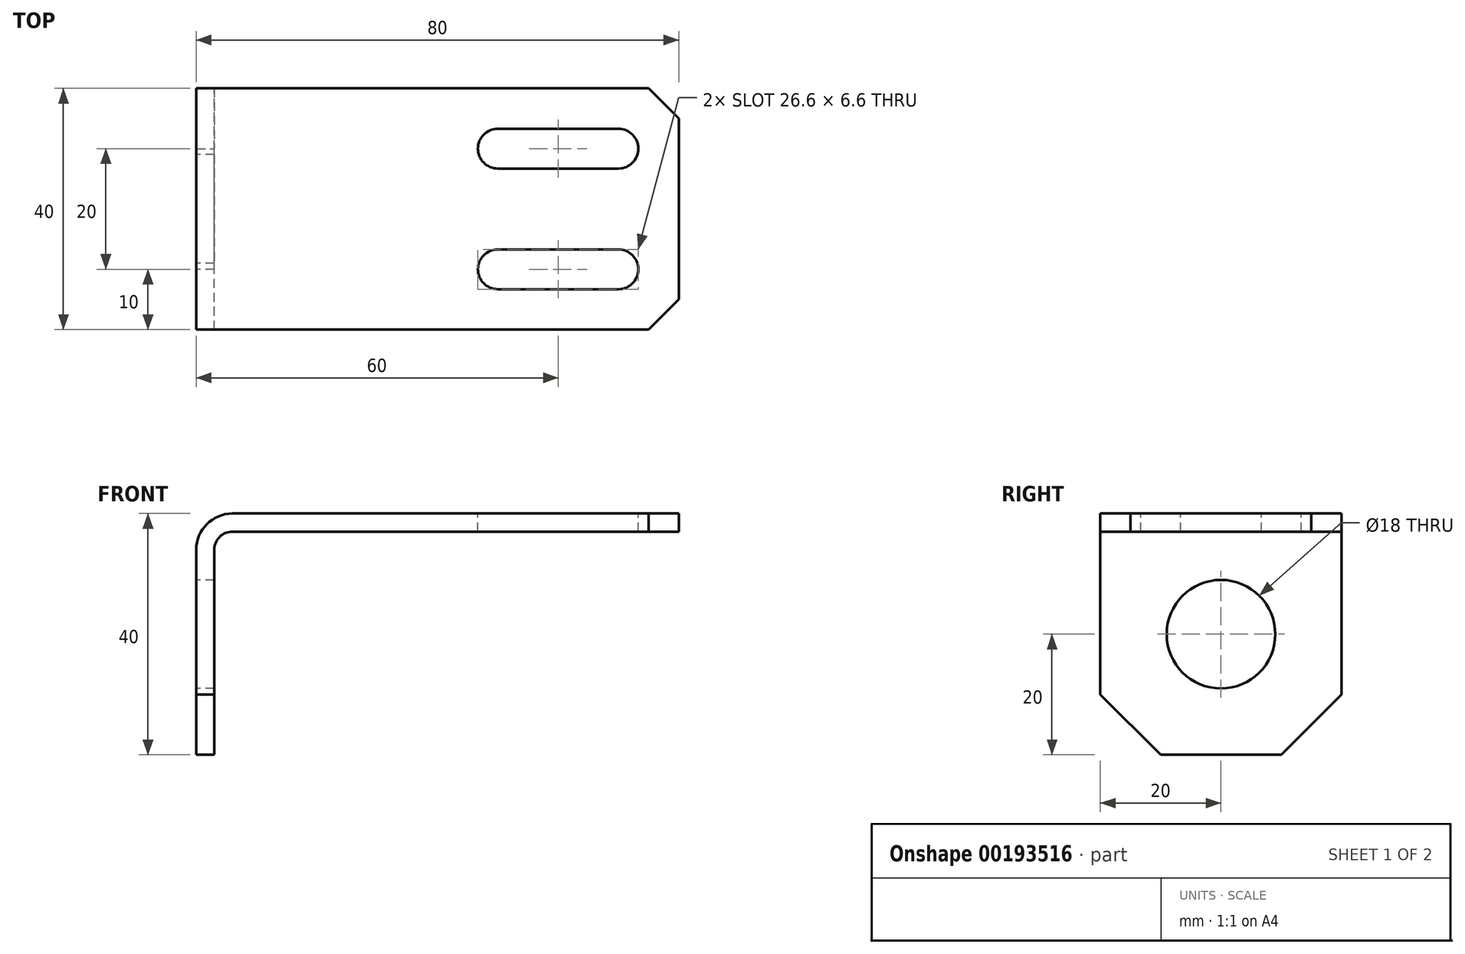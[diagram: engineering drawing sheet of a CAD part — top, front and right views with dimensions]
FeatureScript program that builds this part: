
annotation { "Feature Type Name" : "Feature", "Feature Type Description" : "" }
export const myFeature = defineFeature(function(context is Context, id is Id, definition is map)
    precondition{}
    {
        {
            var Q0;
            Q0=qCreatedBy(makeId("Front.planeOp"),FACE);
            var sketch = newSketch(context, id + "F0", { "sketchPlane" : qUnion([Q0])});
            skLineSegment(sketch, "E0", {"start": v(0, 0) * mm, "end": v(-74, 0) * mm});
            skLineSegment(sketch, "E1", {"start": v(-80, -6) * mm, "end": v(-80, -40) * mm});
            skLineSegment(sketch, "E2", {"start": v(-80, -40) * mm, "end": v(-77, -40) * mm});
            skLineSegment(sketch, "E3", {"start": v(-77, -40) * mm, "end": v(-77, -6) * mm});
            skLineSegment(sketch, "E4", {"start": v(-74, -3) * mm, "end": v(0, -3) * mm});
            skLineSegment(sketch, "E5", {"start": v(0, -3) * mm, "end": v(0, 0) * mm});
            skPoint(sketch, "E6.visualSharp", {"position": v(-77, -3) * mm});
            skArc(sketch, "E6.filletArc", {"start": v(-74, -3) * mm, "mid": v(-76.12, -3.88) * mm, "end": v(-77, -6) * mm});
            skPoint(sketch, "E7.visualSharp", {"position": v(-80, 0) * mm});
            skArc(sketch, "E7.filletArc", {"start": v(-74, 0) * mm, "mid": v(-78.24, -1.76) * mm, "end": v(-80, -6) * mm});
            skLineSegment(sketch, "E8", {"start": v(0, -1.5) * mm, "end": v(-74, -1.5) * mm, "construction": true});
            skLineSegment(sketch, "E9", {"start": v(-78.5, -6) * mm, "end": v(-78.5, -40) * mm, "construction": true});
            skPoint(sketch, "E10.visualSharp", {"position": v(-78.5, -1.5) * mm});
            skArc(sketch, "E10.filletArc", {"start": v(-74, -1.5) * mm, "mid": v(-77.18, -2.82) * mm, "end": v(-78.5, -6) * mm, "construction": true});
            skSolve(sketch);
        }
        {
            var Q0;
            Q0 = qSketchRegion(id + "F0", true);
            extrude(context, id + "F1", {"entities" : qUnion([Q0]), "endBound" : BoundingType.SYMMETRIC, "depth" : 40 * mm});
        }
        {
            var Q0;
            Q0=makeQuery(id+"F1.opExtrude","SWEPT_FACE",FACE,{"disambiguationData":[OSD([sQuery(id+"F0.wireOp",EDGE,"E1")])]});
            var sketch = newSketch(context, id + "F2", { "sketchPlane" : qUnion([Q0])});
            skLineSegment(sketch, "E11", {"start": v(0, -20) * mm, "end": v(0, 0) * mm, "construction": true});
            skPoint(sketch, "E11.endSnap0", {"position": v(0, -6) * mm});
            skCircle(sketch, "E12", {"center": v(0, -20) * mm, "radius": 9 * mm});
            skSolve(sketch);
        }
        {
            var Q0;
            Q0=makeQuery(id+"F2.imprint","IMPRINT",FACE,{"disambiguationData":[TD([[makeQuery(id+"F2.imprint","IMPRINT",EDGE,{"derivedFrom":sQuery(id+"F2.wireOp",EDGE,"E12")}),1.0]])]});
            extrude(context, id + "F3", {"entities" : qUnion([Q0]), "operationType" : NewBodyOperationType.REMOVE, "oppositeDirection" : true, "depth" : 4 * mm});
        }
        {
            var Q0;
            Q0=makeQuery(id+"F1.opExtrude","CAP_EDGE",EDGE,{"disambiguationData":[OSD([sQuery(id+"F0.wireOp",EDGE,"E2")])],"isStart":false});
            var Q1;
            Q1=makeQuery(id+"F1.opExtrude","CAP_EDGE",EDGE,{"disambiguationData":[OSD([sQuery(id+"F0.wireOp",EDGE,"E2")])],"isStart":true});
            chamfer(context, id + "F4", {"entities" : qUnion([Q0, Q1]), "width" : 10 * mm, "tangentPropagation" : true});
        }
        {
            var Q0;
            Q0=makeQuery(id+"F1.opExtrude","SWEPT_FACE",FACE,{"disambiguationData":[OSD([sQuery(id+"F0.wireOp",EDGE,"E0")])]});
            var sketch = newSketch(context, id + "F5", { "sketchPlane" : qUnion([Q0])});
            skLineSegment(sketch, "E13", {"start": v(0, 0) * mm, "end": v(-68.47, 0) * mm, "construction": true});
            skPoint(sketch, "E13.endSnap0", {"position": v(-74, 0) * mm});
            skLineSegment(sketch, "E14", {"start": v(0, -10) * mm, "end": v(-10, -10) * mm, "construction": true});
            skCircle(sketch, "E15", {"center": v(-10, -10) * mm, "radius": 3.3 * mm, "construction": true});
            skLineSegment(sketch, "E16", {"start": v(-10, -10) * mm, "end": v(-30, -10) * mm, "construction": true});
            skCircle(sketch, "E17", {"center": v(-30, -10) * mm, "radius": 3.3 * mm, "construction": true});
            skLineSegment(sketch, "E18", {"start": v(-30, -6.7) * mm, "end": v(-10, -6.7) * mm});
            skLineSegment(sketch, "E19", {"start": v(-30, -10) * mm, "end": v(-30, -13.3) * mm, "construction": true});
            skLineSegment(sketch, "E20", {"start": v(-30, -13.3) * mm, "end": v(-10, -13.3) * mm});
            skArc(sketch, "E21", {"start": v(-30, -6.7) * mm, "mid": v(-33.3, -10) * mm, "end": v(-30, -13.3) * mm});
            skArc(sketch, "E22", {"start": v(-10, -13.3) * mm, "mid": v(-6.7, -10) * mm, "end": v(-10, -6.7) * mm});
            skLineSegment(sketch, "E23.MirrorCS", {"start": v(-30, 6.7) * mm, "end": v(-10, 6.7) * mm});
            skCircle(sketch, "E24.MirrorC", {"center": v(-30, 10) * mm, "radius": 3.3 * mm, "construction": true});
            skLineSegment(sketch, "E25.MirrorCS", {"start": v(-30, 13.3) * mm, "end": v(-10, 13.3) * mm});
            skCircle(sketch, "E26.MirrorC", {"center": v(-10, 10) * mm, "radius": 3.3 * mm, "construction": true});
            skArc(sketch, "E27.MirrorCS", {"start": v(-10, 13.3) * mm, "mid": v(-6.7, 10) * mm, "end": v(-10, 6.7) * mm});
            skArc(sketch, "E28.MirrorCS", {"start": v(-30, 6.7) * mm, "mid": v(-33.3, 10) * mm, "end": v(-30, 13.3) * mm});
            skSolve(sketch);
        }
        {
            var Q0;
            Q0 = qSketchRegion(id + "F5", true);
            extrude(context, id + "F6", {"entities" : qUnion([Q0]), "operationType" : NewBodyOperationType.REMOVE, "oppositeDirection" : true, "depth" : 3 * mm});
        }
        {
            var Q0;
            Q0=makeQuery(id+"F1.opExtrude","CAP_EDGE",EDGE,{"disambiguationData":[OSD([sQuery(id+"F0.wireOp",EDGE,"E5")])],"isStart":false});
            var Q1;
            Q1=makeQuery(id+"F1.opExtrude","CAP_EDGE",EDGE,{"disambiguationData":[OSD([sQuery(id+"F0.wireOp",EDGE,"E5")])],"isStart":true});
            chamfer(context, id + "F7", {"entities" : qUnion([Q0, Q1]), "width" : 5 * mm, "tangentPropagation" : true});
        }
    });
